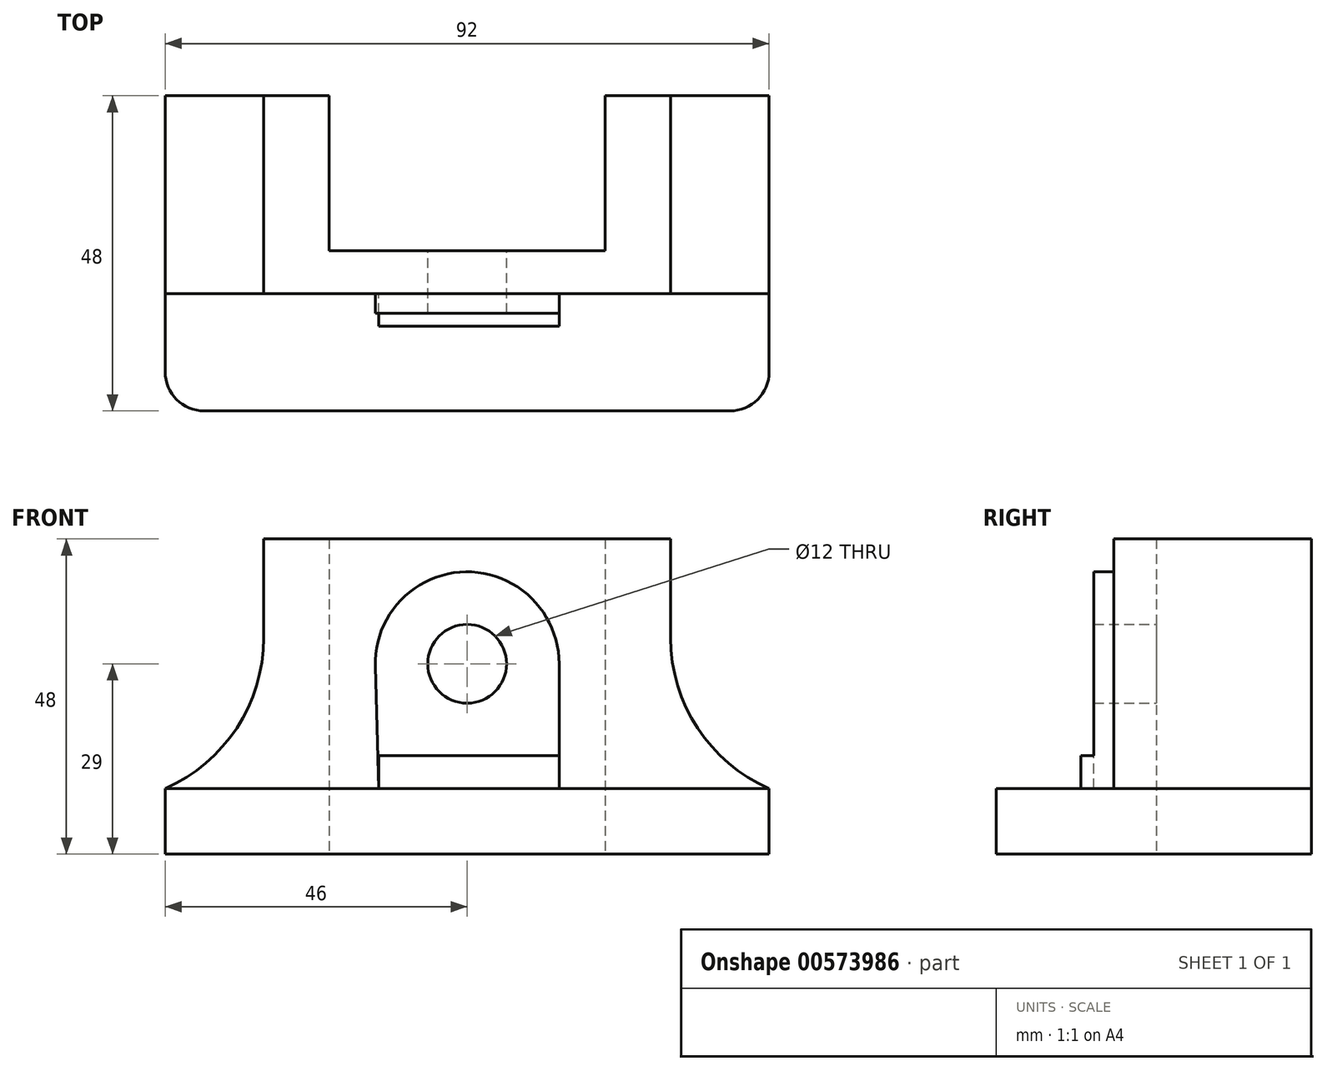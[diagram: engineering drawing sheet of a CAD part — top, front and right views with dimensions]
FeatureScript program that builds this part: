
annotation { "Feature Type Name" : "Feature", "Feature Type Description" : "" }
export const myFeature = defineFeature(function(context is Context, id is Id, definition is map)
    precondition{}
    {
        {
            var Q0;
            Q0=qCreatedBy(makeId("Top.planeOp"),FACE);
            var sketch = newSketch(context, id + "F0", { "sketchPlane" : qUnion([Q0])});
            skLineSegment(sketch, "E0.bottom", {"start": v(46, 30) * mm, "end": v(31, 30) * mm});
            skLineSegment(sketch, "E0.top", {"start": v(46, -18) * mm, "end": v(-46, -18) * mm});
            skLineSegment(sketch, "E0.left", {"start": v(46, 30) * mm, "end": v(46, -18) * mm});
            skLineSegment(sketch, "E0.right", {"start": v(-46, 30) * mm, "end": v(-46, -18) * mm});
            skPoint(sketch, "E0.middle", {"position": v(0, 0) * mm});
            skPoint(sketch, "E1.middle", {"position": v(0, 14.94) * mm});
            skLineSegment(sketch, "E2.trimOffspring", {"start": v(-31, 30) * mm, "end": v(-46, 30) * mm});
            skPoint(sketch, "E1.right.start.orphan", {"position": v(-31, -0.11) * mm});
            skPoint(sketch, "E1.left.end.orphan", {"position": v(31, 30) * mm});
            skPoint(sketch, "E1.left.start.orphan", {"position": v(31, -0.11) * mm});
            skLineSegment(sketch, "E3", {"start": v(-31, 30) * mm, "end": v(-31, -0.11) * mm});
            skLineSegment(sketch, "E4", {"start": v(31, -0.11) * mm, "end": v(31, 30) * mm});
            skLineSegment(sketch, "E5", {"start": v(-31, -0.11) * mm, "end": v(31, -0.11) * mm});
            skLineSegment(sketch, "E6.bottom", {"start": v(-31, 30) * mm, "end": v(-21, 30) * mm});
            skLineSegment(sketch, "E6.right", {"start": v(31, 30) * mm, "end": v(31, -0.11) * mm});
            skLineSegment(sketch, "E7.top", {"start": v(-21, 6.4) * mm, "end": v(21, 6.4) * mm});
            skLineSegment(sketch, "E7.left", {"start": v(-21, 30) * mm, "end": v(-21, 6.4) * mm});
            skLineSegment(sketch, "E7.right", {"start": v(21, 30) * mm, "end": v(21, 6.4) * mm});
            skLineSegment(sketch, "E8.trimOffspring", {"start": v(21, 30) * mm, "end": v(31, 30) * mm});
            skLineSegment(sketch, "E9", {"start": v(0, 53.87) * mm, "end": v(0, -33.71) * mm, "construction": true});
            skSolve(sketch);
        }
        {
            var Q0;
            Q0=qCreatedBy(makeId("Top.planeOp"),FACE);
            var sketch = newSketch(context, id + "F1", { "sketchPlane" : qUnion([Q0])});
            skLineSegment(sketch, "E10.0.0", {"start": v(31, 30) * mm, "end": v(21, 30) * mm});
            skLineSegment(sketch, "E10.0.1", {"start": v(21, 30) * mm, "end": v(21, 6.4) * mm});
            skLineSegment(sketch, "E10.0.2", {"start": v(21, 6.4) * mm, "end": v(-21, 6.4) * mm});
            skLineSegment(sketch, "E10.0.3", {"start": v(-21, 6.4) * mm, "end": v(-21, 30) * mm});
            skLineSegment(sketch, "E10.0.4", {"start": v(-21, 30) * mm, "end": v(-31, 30) * mm});
            skLineSegment(sketch, "E10.0.5", {"start": v(-31, 30) * mm, "end": v(-31, -0.11) * mm});
            skLineSegment(sketch, "E10.0.6", {"start": v(-31, -0.11) * mm, "end": v(31, -0.11) * mm});
            skLineSegment(sketch, "E10.0.7", {"start": v(31, -0.11) * mm, "end": v(31, 30) * mm});
            skSolve(sketch);
        }
        {
            var Q0;
            Q0 = qSketchRegion(id + "F0", true);
            extrude(context, id + "F2", {"entities" : qUnion([Q0]), "depth" : 10 * mm, "offsetDistance" : 25 * mm});
        }
        {
            var Q0;
            Q0 = qSketchRegion(id + "F1", true);
            extrude(context, id + "F3", {"entities" : qUnion([Q0]), "operationType" : NewBodyOperationType.ADD, "depth" : 48 * mm, "offsetDistance" : 25 * mm});
        }
        {
            var Q0;
            Q0=makeQuery(id+"F3.opExtrude","SWEPT_FACE",FACE,{"disambiguationData":[OSD([sQuery(id+"F1.wireOp",EDGE,"E10.0.6")])]});
            var sketch = newSketch(context, id + "F4", { "sketchPlane" : qUnion([Q0])});
            skCircle(sketch, "E11", {"center": v(0, 29) * mm, "radius": 6 * mm});
            skArc(sketch, "E12", {"start": v(14, 29) * mm, "mid": v(-0.2, 43) * mm, "end": v(-14, 28.61) * mm});
            skLineSegment(sketch, "E13", {"start": v(-14, 28.61) * mm, "end": v(-13.48, 10) * mm});
            skLineSegment(sketch, "E14", {"start": v(14, 29) * mm, "end": v(14, 10) * mm});
            skSolve(sketch);
        }
        {
            var Q0;
            Q0=makeQuery(id+"F4.imprint","IMPRINT",FACE,{"disambiguationData":[TD([[makeQuery(id+"F4.imprint","IMPRINT",EDGE,{"derivedFrom":sQuery(id+"F4.wireOp",EDGE,"E11")}),-1.0]])]});
            extrude(context, id + "F5", {"entities" : qUnion([Q0]), "operationType" : NewBodyOperationType.ADD, "depth" : 3 * mm, "offsetDistance" : 25 * mm});
        }
        {
            var Q0;
            Q0=makeQuery(id+"F5.opExtrude","CAP_FACE",FACE,{"disambiguationData":[OSD([sQuery(id+"F0.wireOp",EDGE,"E0.bottom"),sQuery(id+"F0.wireOp",EDGE,"E0.top"),sQuery(id+"F0.wireOp",EDGE,"E0.left"),sQuery(id+"F0.wireOp",EDGE,"E0.right"),sQuery(id+"F0.wireOp",EDGE,"E2.trimOffspring"),sQuery(id+"F0.wireOp",EDGE,"E6.bottom"),sQuery(id+"F0.wireOp",EDGE,"E7.top"),sQuery(id+"F0.wireOp",EDGE,"E7.left"),sQuery(id+"F0.wireOp",EDGE,"E7.right"),sQuery(id+"F0.wireOp",EDGE,"E8.trimOffspring"),sQuery(id+"F1.wireOp",EDGE,"E10.0.6"),sQuery(id+"F4.wireOp",EDGE,"E11"),sQuery(id+"F4.wireOp",EDGE,"E12"),sQuery(id+"F4.wireOp",EDGE,"E13"),sQuery(id+"F4.wireOp",EDGE,"E14")])],"isStart":false});
            var sketch = newSketch(context, id + "F6", { "sketchPlane" : qUnion([Q0])});
            skLineSegment(sketch, "E15.bottom", {"start": v(-13.48, 10) * mm, "end": v(14, 10) * mm});
            skLineSegment(sketch, "E15.top", {"start": v(-13.48, 15) * mm, "end": v(14, 15) * mm});
            skLineSegment(sketch, "E15.left", {"start": v(-13.48, 10) * mm, "end": v(-13.48, 15) * mm});
            skLineSegment(sketch, "E15.right", {"start": v(14, 10) * mm, "end": v(14, 15) * mm});
            skPoint(sketch, "E16", {"position": v(0, 29) * mm});
            skSolve(sketch);
        }
        {
            var Q0;
            Q0=makeQuery(id+"F6.imprint","IMPRINT",FACE,{"disambiguationData":[TD([[makeQuery(id+"F6.imprint","IMPRINT",EDGE,{"derivedFrom":sQuery(id+"F6.wireOp",EDGE,"E15.bottom")}),-1.0]])]});
            extrude(context, id + "F7", {"entities" : qUnion([Q0]), "operationType" : NewBodyOperationType.ADD, "depth" : 2 * mm, "offsetDistance" : 25 * mm});
        }
        {
            var Q0;
            Q0=makeQuery(id+"F5.boolean.opBoolean","SPLIT",FACE,{"disambiguationData":[TD([makeQuery(id+"F5.opExtrude","SWEPT_FACE",FACE,{"disambiguationData":[OSD([sQuery(id+"F4.wireOp",EDGE,"E11")])]})])],"derivedFrom":makeQuery(id+"F3.opExtrude","SWEPT_FACE",FACE,{"disambiguationData":[OSD([sQuery(id+"F1.wireOp",EDGE,"E10.0.6")])]})});
            extrude(context, id + "F8", {"entities" : qUnion([Q0]), "operationType" : NewBodyOperationType.REMOVE, "oppositeDirection" : true, "depth" : 20 * mm, "offsetDistance" : 25 * mm});
        }
        {
            var Q0;
            Q0=makeQuery(id+"F3.boolean.opBoolean","INTERSECT",EDGE,{"derivedFrom":[makeQuery(id+"F2.opExtrude","CAP_FACE",FACE,{"disambiguationData":[OSD([sQuery(id+"F0.wireOp",EDGE,"E0.bottom"),sQuery(id+"F0.wireOp",EDGE,"E0.top"),sQuery(id+"F0.wireOp",EDGE,"E0.left"),sQuery(id+"F0.wireOp",EDGE,"E0.right"),sQuery(id+"F0.wireOp",EDGE,"E2.trimOffspring"),sQuery(id+"F0.wireOp",EDGE,"E6.bottom"),sQuery(id+"F0.wireOp",EDGE,"E7.top"),sQuery(id+"F0.wireOp",EDGE,"E7.left"),sQuery(id+"F0.wireOp",EDGE,"E7.right"),sQuery(id+"F0.wireOp",EDGE,"E8.trimOffspring")])],"isStart":false}),makeQuery(id+"F3.opExtrude","SWEPT_FACE",FACE,{"disambiguationData":[OSD([sQuery(id+"F1.wireOp",EDGE,"E10.0.7")])]})]});
            var Q1;
            Q1=makeQuery(id+"F3.boolean.opBoolean","INTERSECT",EDGE,{"derivedFrom":[makeQuery(id+"F2.opExtrude","CAP_FACE",FACE,{"disambiguationData":[OSD([sQuery(id+"F0.wireOp",EDGE,"E0.bottom"),sQuery(id+"F0.wireOp",EDGE,"E0.top"),sQuery(id+"F0.wireOp",EDGE,"E0.left"),sQuery(id+"F0.wireOp",EDGE,"E0.right"),sQuery(id+"F0.wireOp",EDGE,"E2.trimOffspring"),sQuery(id+"F0.wireOp",EDGE,"E6.bottom"),sQuery(id+"F0.wireOp",EDGE,"E7.top"),sQuery(id+"F0.wireOp",EDGE,"E7.left"),sQuery(id+"F0.wireOp",EDGE,"E7.right"),sQuery(id+"F0.wireOp",EDGE,"E8.trimOffspring")])],"isStart":false}),makeQuery(id+"F3.opExtrude","SWEPT_FACE",FACE,{"disambiguationData":[OSD([sQuery(id+"F1.wireOp",EDGE,"E10.0.5")])]})]});
            fillet(context, id + "F9", {"entities" : qUnion([Q0, Q1]), "radius" : 25 * mm, "tangentPropagation" : true, "allowEdgeOverflow" : false});
        }
        {
            var Q0;
            Q0=makeQuery(id+"F2.opExtrude","SWEPT_EDGE",EDGE,{"disambiguationData":[OSD([sQuery(id+"F0.wireOp",EDGE,"E0.top"),sQuery(id+"F0.wireOp",EDGE,"E0.right")])]});
            var Q1;
            Q1=makeQuery(id+"F2.opExtrude","SWEPT_EDGE",EDGE,{"disambiguationData":[OSD([sQuery(id+"F0.wireOp",EDGE,"E0.top"),sQuery(id+"F0.wireOp",EDGE,"E0.left")])]});
            fillet(context, id + "F10", {"entities" : qUnion([Q0, Q1]), "radius" : 6 * mm, "tangentPropagation" : true, "allowEdgeOverflow" : false});
        }
    });
